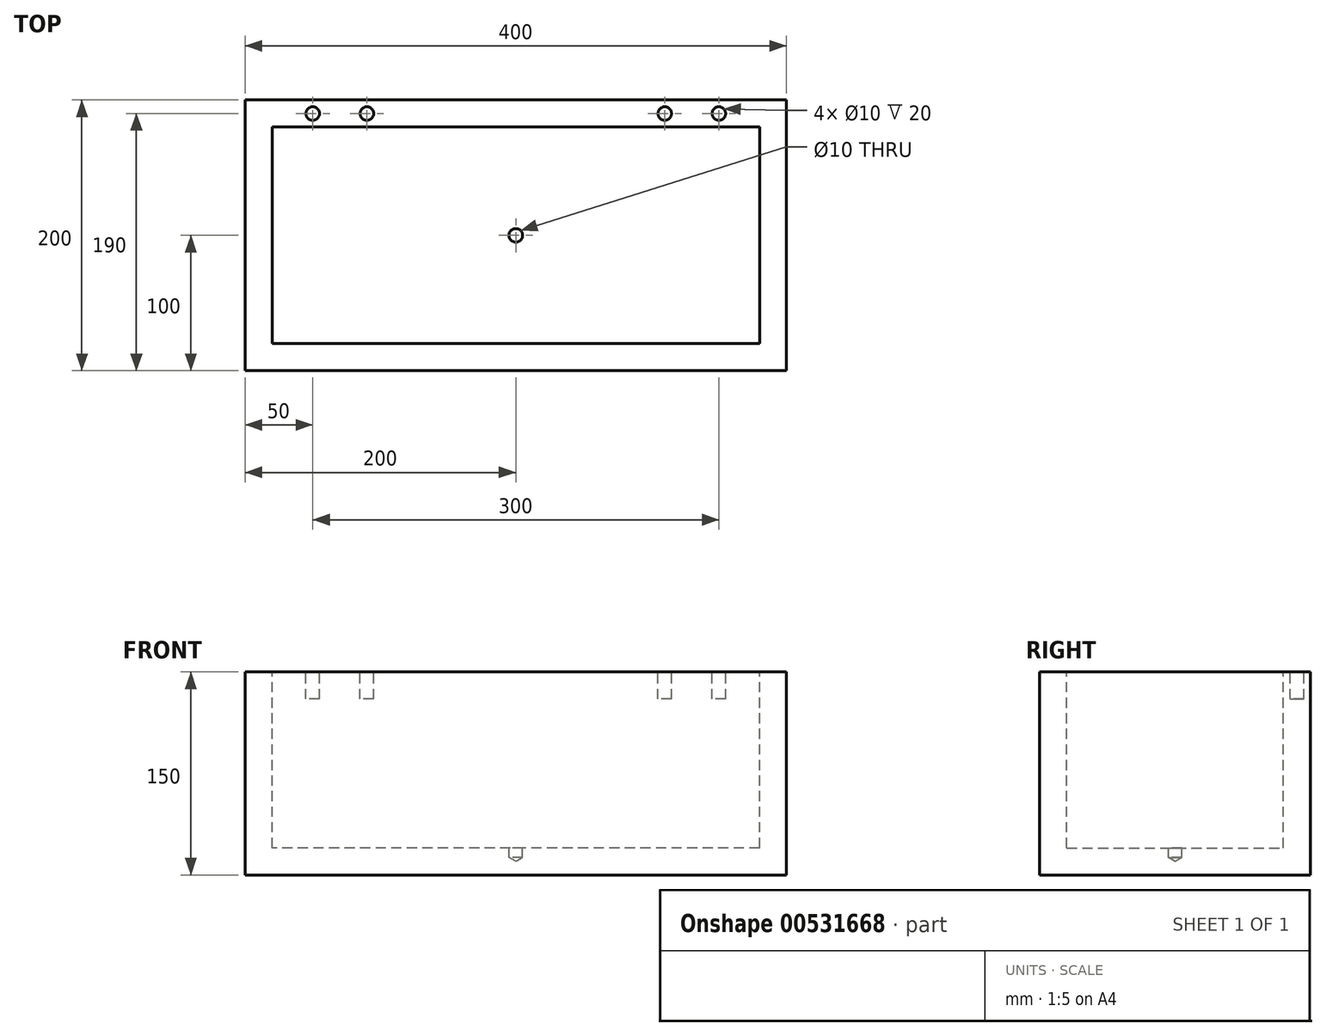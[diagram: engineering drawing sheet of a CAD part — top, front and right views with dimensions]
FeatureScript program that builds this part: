
annotation { "Feature Type Name" : "Feature", "Feature Type Description" : "" }
export const myFeature = defineFeature(function(context is Context, id is Id, definition is map)
    precondition{}
    {
        {
            var Q0;
            Q0=qCreatedBy(makeId("Top.planeOp"),FACE);
            var sketch = newSketch(context, id + "F0", { "sketchPlane" : qUnion([Q0])});
            skLineSegment(sketch, "E0.bottom", {"start": v(200, -100) * mm, "end": v(-200, -100) * mm});
            skLineSegment(sketch, "E0.top", {"start": v(200, 100) * mm, "end": v(-200, 100) * mm});
            skLineSegment(sketch, "E0.left", {"start": v(200, -100) * mm, "end": v(200, 100) * mm});
            skLineSegment(sketch, "E0.right", {"start": v(-200, -100) * mm, "end": v(-200, 100) * mm});
            skPoint(sketch, "E0.middle", {"position": v(0, 0) * mm});
            skSolve(sketch);
        }
        {
            var Q0;
            Q0=qSketchRegion(id+"F0",true);
            extrude(context, id + "F1", {"entities" : qUnion([Q0]), "depth" : 150 * mm, "offsetDistance" : 25 * mm});
        }
        {
            var Q0;
            Q0=makeQuery(id+"F1.opExtrude","CAP_FACE",FACE,{"disambiguationData":[OSD([sQuery(id+"F0.wireOp",EDGE,"E0.bottom"),sQuery(id+"F0.wireOp",EDGE,"E0.top"),sQuery(id+"F0.wireOp",EDGE,"E0.left"),sQuery(id+"F0.wireOp",EDGE,"E0.right")])],"isStart":false});
            var sketch = newSketch(context, id + "F2", { "sketchPlane" : qUnion([Q0])});
            skLineSegment(sketch, "E1.bottom", {"start": v(180, -80) * mm, "end": v(-180, -80) * mm});
            skLineSegment(sketch, "E1.top", {"start": v(180, 80) * mm, "end": v(-180, 80) * mm});
            skLineSegment(sketch, "E1.left", {"start": v(180, -80) * mm, "end": v(180, 80) * mm});
            skLineSegment(sketch, "E1.right", {"start": v(-180, -80) * mm, "end": v(-180, 80) * mm});
            skPoint(sketch, "E1.middle", {"position": v(0, 0) * mm});
            skSolve(sketch);
        }
        {
            var Q0;
            Q0=makeQuery(id+"F2.imprint","IMPRINT",FACE,{"disambiguationData":[TD([[makeQuery(id+"F2.imprint","IMPRINT",EDGE,{"derivedFrom":sQuery(id+"F2.wireOp",EDGE,"E1.bottom")}),-1.0]])]});
            extrude(context, id + "F3", {"entities" : qUnion([Q0]), "operationType" : NewBodyOperationType.REMOVE, "oppositeDirection" : true, "depth" : 130 * mm});
        }
        {
            var Q0;
            Q0=makeQuery(id+"F1.opExtrude","CAP_FACE",FACE,{"disambiguationData":[OSD([sQuery(id+"F0.wireOp",EDGE,"E0.bottom"),sQuery(id+"F0.wireOp",EDGE,"E0.top"),sQuery(id+"F0.wireOp",EDGE,"E0.left"),sQuery(id+"F0.wireOp",EDGE,"E0.right")])],"isStart":false});
            var sketch = newSketch(context, id + "F4", { "sketchPlane" : qUnion([Q0])});
            skCircle(sketch, "E2", {"center": v(-150, 90) * mm, "radius": 5 * mm});
            skCircle(sketch, "E3", {"center": v(-110, 90) * mm, "radius": 5 * mm});
            skLineSegment(sketch, "E4", {"start": v(0, 80) * mm, "end": v(0, 100) * mm, "construction": true});
            skCircle(sketch, "E5.MirrorC", {"center": v(110, 90) * mm, "radius": 5 * mm});
            skCircle(sketch, "E6.MirrorC", {"center": v(150, 90) * mm, "radius": 5 * mm});
            skSolve(sketch);
        }
        {
            var Q0;
            Q0=qSketchRegion(id+"F4",true);
            extrude(context, id + "F5", {"entities" : qUnion([Q0]), "operationType" : NewBodyOperationType.REMOVE, "oppositeDirection" : true, "depth" : 20 * mm});
        }
        {
            var Q0;
            Q0=makeQuery(id+"F3.boolean.opBoolean","COPY",FACE,{"derivedFrom":makeQuery(id+"F3.opExtrude","CAP_FACE",FACE,{"disambiguationData":[OSD([sQuery(id+"F2.wireOp",EDGE,"E1.bottom"),sQuery(id+"F2.wireOp",EDGE,"E1.top"),sQuery(id+"F2.wireOp",EDGE,"E1.left"),sQuery(id+"F2.wireOp",EDGE,"E1.right")])],"isStart":false})});
            var sketch = newSketch(context, id + "F6", { "sketchPlane" : qUnion([Q0])});
            skCircle(sketch, "E7", {"center": v(0, 0) * mm, "radius": 5 * mm});
            skSolve(sketch);
        }
        {
            var Q0;
            Q0=sQuery(id+"F6.wireOp",VERTEX,"E7.center");
            var Q1;
            Q1=makeQuery(id+"F1.opExtrude","SWEPT_BODY",BODY,{"disambiguationData":[OSD([sQuery(id+"F0.wireOp",EDGE,"E0.bottom"),sQuery(id+"F0.wireOp",EDGE,"E0.top"),sQuery(id+"F0.wireOp",EDGE,"E0.left"),sQuery(id+"F0.wireOp",EDGE,"E0.right")])]});
            hole(context, id + "F7", {"style" : HoleStyle.SIMPLE, "endStyle" : HoleEndStyle.BLIND, "holeDiameter" : 10 * mm, "majorDiameter" : 5 * mm, "holeDepth" : 7 * mm, "isTappedThrough" : true, "tappedDepth" : 12 * mm, "tapClearance" : 3, "locations" : qUnion([Q0]), "scope" : qUnion([Q1])});
        }
    });
